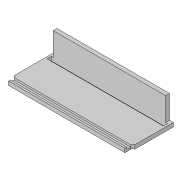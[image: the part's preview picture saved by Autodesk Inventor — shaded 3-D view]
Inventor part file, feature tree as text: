
AUTODESK INVENTOR PART (.ipt)
format: ipt  version: 2018.3 (Build 223284000, 284)  size: 144,384 bytes
history: native  units: in
note: dims shown in document units (in); Inventor stores cm internally (conversion verified against a paired STEP export)
features: extrude x5, sketch x5, fillet x1
ambient origin geometry x8: Origin, YZ Plane, XZ Plane, XY Plane, X Axis, Y Axis, Z Axis, Center Point
bodies: Solid1 (feature_tree)
feature tree (11):
  extrude  "Extrusion1"  Depth=1.5in
  extrude  "Extrusion2"  Depth=0.126in
  extrude  "Extrusion3"  Depth=0.0625in
  extrude  "Extrusion4"  Depth=0.135in
  fillet  "Fillet1"  Radius=0.125in
  extrude  "Extrusion5"  Depth=0.135in
  sketch  "Sketch1"  dims[d0=3.875in d1=1.5in]
  sketch  "Sketch2"  dims[d2=0.125in d3=0.0in d4=0.126in]
  sketch  "Sketch3"  dims[d5=0.0625in d8=3.375in]
  sketch  "Sketch4"  dims[d9=0.0625in d10=0.135in d11=0.125in]
  sketch  "Sketch5"  dims[d12=0.0625in d13=0.0in d15=0.135in d16=0.125in d17=0.0625in d18=0.5in d19=0.0in d20=0.0625in d21=0.0625in d22=0.25in d23=0.25in d24=0.0625in d25=0.5in d26=0.0in d27=0.0625in d29=0.75in d30=0.0in d31=0.125in d32=0.126in d33=0.126in]
